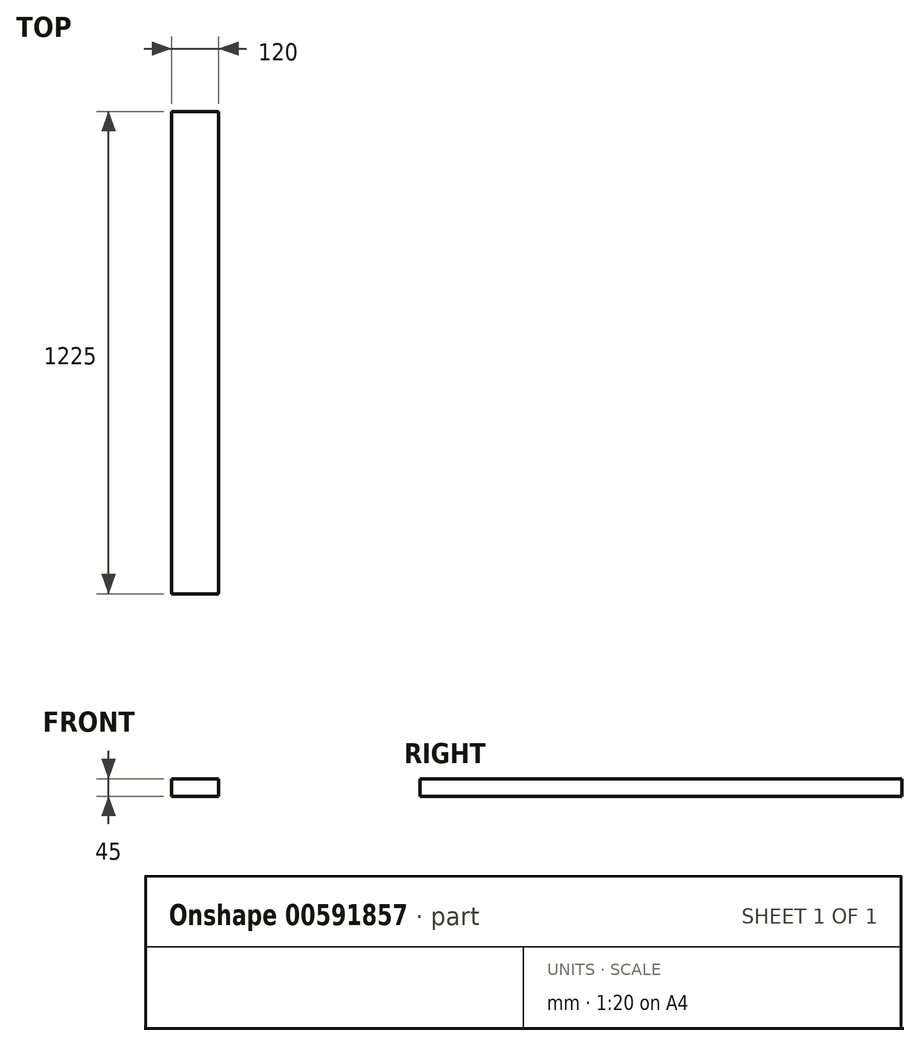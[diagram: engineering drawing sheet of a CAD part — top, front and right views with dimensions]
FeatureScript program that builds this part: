
annotation { "Feature Type Name" : "Feature", "Feature Type Description" : "" }
export const myFeature = defineFeature(function(context is Context, id is Id, definition is map)
    precondition{}
    {
        {
            var Q0;
            Q0=qCreatedBy(makeId("Top.planeOp"),FACE);
            var sketch = newSketch(context, id + "F0", { "sketchPlane" : qUnion([Q0])});
            skLineSegment(sketch, "E0.bottom", {"start": v(0, 0) * mm, "end": v(-120, 0) * mm});
            skLineSegment(sketch, "E0.top", {"start": v(0, 1225) * mm, "end": v(-120, 1225) * mm});
            skLineSegment(sketch, "E0.left", {"start": v(0, 0) * mm, "end": v(0, 1225) * mm});
            skLineSegment(sketch, "E0.right", {"start": v(-120, 0) * mm, "end": v(-120, 1225) * mm});
            skSolve(sketch);
        }
        {
            var Q0;
            Q0=makeQuery(id+"F0.imprint","IMPRINT",FACE,{"disambiguationData":[TD([[makeQuery(id+"F0.imprint","IMPRINT",EDGE,{"derivedFrom":sQuery(id+"F0.wireOp",EDGE,"E0.bottom")}),-1.0]])]});
            extrude(context, id + "F1", {"entities" : qUnion([Q0]), "depth" : 45 * mm, "offsetDistance" : 25 * mm});
        }
    });
